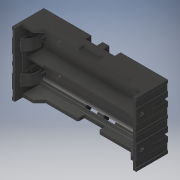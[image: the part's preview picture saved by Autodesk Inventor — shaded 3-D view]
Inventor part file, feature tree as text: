
AUTODESK INVENTOR PART (.ipt)
format: ipt  version: 2019 (Build 230136000, 136)  size: 327,168 bytes
history: native  units: mm
features: other x2, extrude x1, sketch x1
ambient origin geometry x8: Origin, YZ Plane, XZ Plane, XY Plane, X Axis, Y Axis, Z Axis, Center Point
bodies: Body1 (feature_tree)
feature tree (4):
  other  "Твердое тело1"
  extrude  "Выдавливание3"  Depth=20.0mm TaperAngle=0.0deg
  sketch  "Эскиз3"
  other  "Corps principal"
